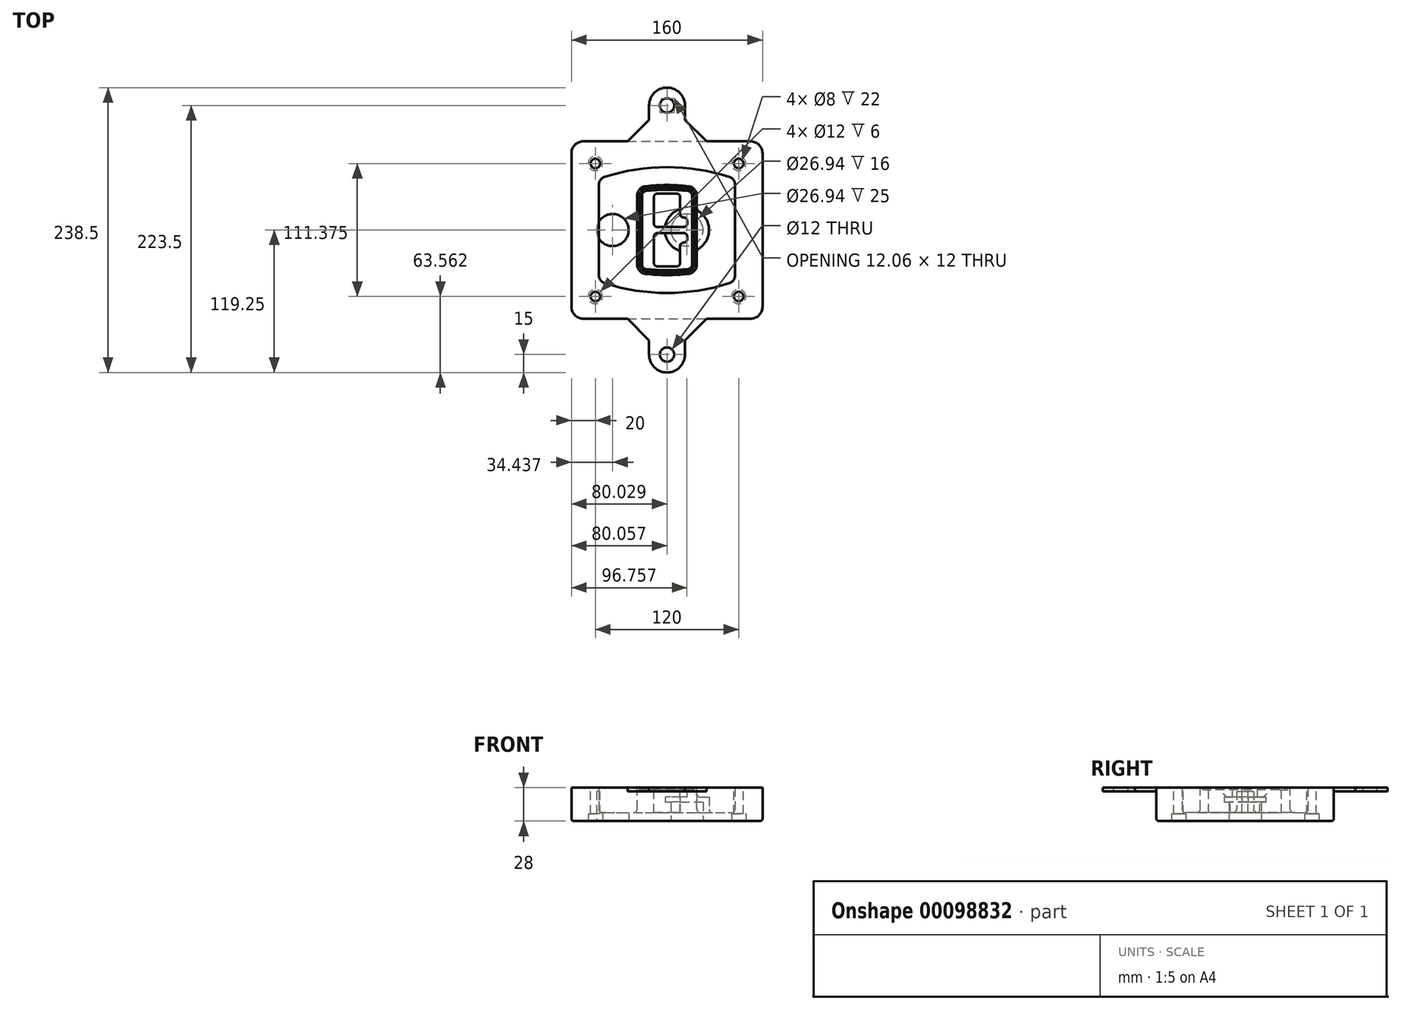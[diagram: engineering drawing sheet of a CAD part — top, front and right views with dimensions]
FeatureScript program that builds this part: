
annotation { "Feature Type Name" : "Feature", "Feature Type Description" : "" }
export const myFeature = defineFeature(function(context is Context, id is Id, definition is map)
    precondition{}
    {
        {
            var Q0;
            Q0=qCreatedBy(makeId("Top.planeOp"),FACE);
            var sketch = newSketch(context, id + "F0", { "sketchPlane" : qUnion([Q0])});
            skPoint(sketch, "E0.rect.middle", {"position": v(0, 0) * mm});
            skLineSegment(sketch, "E1.bottom", {"start": v(-70, -74.25) * mm, "end": v(70, -74.25) * mm});
            skLineSegment(sketch, "E1.top", {"start": v(-70, 74.25) * mm, "end": v(70, 74.25) * mm});
            skLineSegment(sketch, "E1.left", {"start": v(-80, -64.25) * mm, "end": v(-80, 64.25) * mm});
            skLineSegment(sketch, "E1.right", {"start": v(80, -64.25) * mm, "end": v(80, 64.25) * mm});
            skLineSegment(sketch, "E2", {"start": v(-80, 74.25) * mm, "end": v(80, -74.25) * mm, "construction": true});
            skLineSegment(sketch, "E3", {"start": v(80, 74.25) * mm, "end": v(-80, -74.25) * mm, "construction": true});
            skCircle(sketch, "E4", {"center": v(-60, 55.69) * mm, "radius": 4 * mm});
            skCircle(sketch, "E5", {"center": v(60, 55.69) * mm, "radius": 4 * mm});
            skCircle(sketch, "E6", {"center": v(60, -55.69) * mm, "radius": 4 * mm});
            skCircle(sketch, "E7", {"center": v(-60, -55.69) * mm, "radius": 4 * mm});
            skLineSegment(sketch, "E8", {"start": v(-60, 55.69) * mm, "end": v(60, 55.69) * mm, "construction": true});
            skLineSegment(sketch, "E9", {"start": v(60, 55.69) * mm, "end": v(60, -55.69) * mm, "construction": true});
            skLineSegment(sketch, "E10", {"start": v(60, -55.69) * mm, "end": v(-60, -55.69) * mm, "construction": true});
            skLineSegment(sketch, "E11", {"start": v(-60, -55.69) * mm, "end": v(-60, 55.69) * mm, "construction": true});
            skLineSegment(sketch, "E12", {"start": v(-60, 37.87) * mm, "end": v(-60, -37.87) * mm});
            skLineSegment(sketch, "E13", {"start": v(60, 37.87) * mm, "end": v(60, -37.87) * mm});
            skArc(sketch, "E14", {"start": v(53.05, 47.4) * mm, "mid": v(0, 55.69) * mm, "end": v(-53.05, 47.4) * mm});
            skArc(sketch, "E15", {"start": v(-53.05, -47.4) * mm, "mid": v(0, -55.69) * mm, "end": v(53.05, -47.4) * mm});
            skLineSegment(sketch, "E16", {"start": v(-60, 0) * mm, "end": v(60, 0) * mm, "construction": true});
            skPoint(sketch, "E17.visualSharp", {"position": v(-60, -45) * mm});
            skArc(sketch, "E17.filletArc", {"start": v(-60, -37.87) * mm, "mid": v(-58.08, -43.76) * mm, "end": v(-53.05, -47.4) * mm});
            skPoint(sketch, "E18.visualSharp", {"position": v(-60, 45) * mm});
            skArc(sketch, "E18.filletArc", {"start": v(-53.05, 47.4) * mm, "mid": v(-58.08, 43.76) * mm, "end": v(-60, 37.87) * mm});
            skPoint(sketch, "E19.visualSharp", {"position": v(60, 45) * mm});
            skArc(sketch, "E19.filletArc", {"start": v(60, 37.87) * mm, "mid": v(58.08, 43.76) * mm, "end": v(53.05, 47.4) * mm});
            skPoint(sketch, "E20.visualSharp", {"position": v(60, -45) * mm});
            skArc(sketch, "E20.filletArc", {"start": v(53.05, -47.4) * mm, "mid": v(58.08, -43.76) * mm, "end": v(60, -37.87) * mm});
            skPoint(sketch, "E21.visualSharp", {"position": v(-80, 74.25) * mm});
            skArc(sketch, "E21.filletArc", {"start": v(-70, 74.25) * mm, "mid": v(-77.07, 71.32) * mm, "end": v(-80, 64.25) * mm});
            skPoint(sketch, "E22.visualSharp", {"position": v(80, 74.25) * mm});
            skArc(sketch, "E22.filletArc", {"start": v(80, 64.25) * mm, "mid": v(77.07, 71.32) * mm, "end": v(70, 74.25) * mm});
            skPoint(sketch, "E23.visualSharp", {"position": v(80, -74.25) * mm});
            skArc(sketch, "E23.filletArc", {"start": v(70, -74.25) * mm, "mid": v(77.07, -71.32) * mm, "end": v(80, -64.25) * mm});
            skPoint(sketch, "E24.visualSharp", {"position": v(-80, -74.25) * mm});
            skArc(sketch, "E24.filletArc", {"start": v(-80, -64.25) * mm, "mid": v(-77.07, -71.32) * mm, "end": v(-70, -74.25) * mm});
            skArc(sketch, "E25.0", {"start": v(57, 37.87) * mm, "mid": v(55.66, 42) * mm, "end": v(52.14, 44.53) * mm});
            skLineSegment(sketch, "E25.1", {"start": v(57, 37.87) * mm, "end": v(57, -37.87) * mm});
            skArc(sketch, "E25.2", {"start": v(52.14, -44.53) * mm, "mid": v(55.66, -42) * mm, "end": v(57, -37.87) * mm});
            skArc(sketch, "E25.3", {"start": v(-52.14, -44.53) * mm, "mid": v(0, -52.69) * mm, "end": v(52.14, -44.53) * mm});
            skArc(sketch, "E25.4", {"start": v(-57, -37.87) * mm, "mid": v(-55.66, -42) * mm, "end": v(-52.14, -44.53) * mm});
            skArc(sketch, "E25.5", {"start": v(52.14, 44.53) * mm, "mid": v(0, 52.69) * mm, "end": v(-52.14, 44.53) * mm});
            skLineSegment(sketch, "E25.6", {"start": v(-57, 37.87) * mm, "end": v(-57, -37.87) * mm});
            skArc(sketch, "E25.7", {"start": v(-52.14, 44.53) * mm, "mid": v(-55.66, 42) * mm, "end": v(-57, 37.87) * mm});
            skArc(sketch, "E26.0", {"start": v(-54.27, 51.2) * mm, "mid": v(-61.31, 46.12) * mm, "end": v(-64, 37.87) * mm});
            skArc(sketch, "E26.1", {"start": v(54.27, 51.2) * mm, "mid": v(0, 59.69) * mm, "end": v(-54.27, 51.2) * mm});
            skArc(sketch, "E26.2", {"start": v(64, 37.87) * mm, "mid": v(61.31, 46.12) * mm, "end": v(54.27, 51.2) * mm});
            skLineSegment(sketch, "E26.3", {"start": v(64, 37.87) * mm, "end": v(64, -37.87) * mm});
            skArc(sketch, "E26.4", {"start": v(54.27, -51.2) * mm, "mid": v(61.31, -46.12) * mm, "end": v(64, -37.87) * mm});
            skLineSegment(sketch, "E26.5", {"start": v(-64, 37.87) * mm, "end": v(-64, -37.87) * mm});
            skArc(sketch, "E26.6", {"start": v(-54.27, -51.2) * mm, "mid": v(0, -59.69) * mm, "end": v(54.27, -51.2) * mm});
            skArc(sketch, "E26.7", {"start": v(-64, -37.87) * mm, "mid": v(-61.31, -46.12) * mm, "end": v(-54.27, -51.2) * mm});
            skSolve(sketch);
        }
        {
            var Q0;
            Q0=makeQuery(id+"F0.imprint","IMPRINT",FACE,{"disambiguationData":[TD([[makeQuery(id+"F0.imprint","IMPRINT",EDGE,{"derivedFrom":sQuery(id+"F0.wireOp",EDGE,"E1.bottom")}),1.0]])]});
            var Q1;
            Q1=makeQuery(id+"F0.imprint","IMPRINT",FACE,{"disambiguationData":[TD([[makeQuery(id+"F0.imprint","IMPRINT",EDGE,{"derivedFrom":sQuery(id+"F0.wireOp",EDGE,"E12")}),1.0]])]});
            var Q2;
            Q2=makeQuery(id+"F0.imprint","IMPRINT",FACE,{"disambiguationData":[TD([[makeQuery(id+"F0.imprint","IMPRINT",EDGE,{"derivedFrom":sQuery(id+"F0.wireOp",EDGE,"E25.0")}),1.0]])]});
            var Q3;
            Q3=makeQuery(id+"F0.imprint","IMPRINT",FACE,{"disambiguationData":[TD([[makeQuery(id+"F0.imprint","IMPRINT",EDGE,{"derivedFrom":sQuery(id+"F0.wireOp",EDGE,"E12")}),-1.0]])]});
            extrude(context, id + "F1", {"entities" : qUnion([Q0, Q1, Q2, Q3]), "oppositeDirection" : true, "depth" : 25 * mm});
        }
        {
            var Q0;
            Q0=makeQuery(id+"F0.imprint","IMPRINT",FACE,{"disambiguationData":[TD([[makeQuery(id+"F0.imprint","IMPRINT",EDGE,{"derivedFrom":sQuery(id+"F0.wireOp",EDGE,"E12")}),1.0]])]});
            extrude(context, id + "F2", {"entities" : qUnion([Q0]), "operationType" : NewBodyOperationType.ADD, "depth" : 3 * mm});
        }
        {
            var Q0;
            Q0=makeQuery(id+"F0.imprint","IMPRINT",FACE,{"disambiguationData":[TD([[makeQuery(id+"F0.imprint","IMPRINT",EDGE,{"derivedFrom":sQuery(id+"F0.wireOp",EDGE,"E25.0")}),1.0]])]});
            extrude(context, id + "F3", {"entities" : qUnion([Q0]), "operationType" : NewBodyOperationType.REMOVE, "oppositeDirection" : true, "depth" : 18 * mm});
        }
        {
            var Q0;
            Q0=makeQuery(id+"F2.opExtrude","CAP_FACE",FACE,{"disambiguationData":[OSD([sQuery(id+"F0.wireOp",EDGE,"E12"),sQuery(id+"F0.wireOp",EDGE,"E13"),sQuery(id+"F0.wireOp",EDGE,"E14"),sQuery(id+"F0.wireOp",EDGE,"E15"),sQuery(id+"F0.wireOp",EDGE,"E17.filletArc"),sQuery(id+"F0.wireOp",EDGE,"E18.filletArc"),sQuery(id+"F0.wireOp",EDGE,"E19.filletArc"),sQuery(id+"F0.wireOp",EDGE,"E20.filletArc"),sQuery(id+"F0.wireOp",EDGE,"E25.0"),sQuery(id+"F0.wireOp",EDGE,"E25.1"),sQuery(id+"F0.wireOp",EDGE,"E25.2"),sQuery(id+"F0.wireOp",EDGE,"E25.3"),sQuery(id+"F0.wireOp",EDGE,"E25.4"),sQuery(id+"F0.wireOp",EDGE,"E25.5"),sQuery(id+"F0.wireOp",EDGE,"E25.6"),sQuery(id+"F0.wireOp",EDGE,"E25.7")])],"isStart":false});
            var sketch = newSketch(context, id + "F4", { "sketchPlane" : qUnion([Q0])});
            skArc(sketch, "E27.0", {"start": v(-17.92, -36.65) * mm, "mid": v(0, -37.69) * mm, "end": v(17.92, -36.65) * mm});
            skArc(sketch, "E28.0", {"start": v(17.92, 36.65) * mm, "mid": v(0, 37.69) * mm, "end": v(-17.92, 36.65) * mm});
            skLineSegment(sketch, "E29", {"start": v(-25, 28.7) * mm, "end": v(-25, -28.7) * mm});
            skLineSegment(sketch, "E30", {"start": v(25, 28.7) * mm, "end": v(25, -28.7) * mm});
            skLineSegment(sketch, "E31", {"start": v(-25, 35.67) * mm, "end": v(25, 35.67) * mm, "construction": true});
            skLineSegment(sketch, "E32", {"start": v(-25, -35.67) * mm, "end": v(25, -35.67) * mm, "construction": true});
            skPoint(sketch, "E33.visualSharp", {"position": v(-25, 35.67) * mm});
            skArc(sketch, "E33.filletArc", {"start": v(-17.92, 36.65) * mm, "mid": v(-22.97, 34.03) * mm, "end": v(-25, 28.7) * mm});
            skPoint(sketch, "E34.visualSharp", {"position": v(25, 35.67) * mm});
            skArc(sketch, "E34.filletArc", {"start": v(25, 28.7) * mm, "mid": v(22.97, 34.03) * mm, "end": v(17.92, 36.65) * mm});
            skPoint(sketch, "E35.visualSharp", {"position": v(25, -35.67) * mm});
            skArc(sketch, "E35.filletArc", {"start": v(17.92, -36.65) * mm, "mid": v(22.97, -34.03) * mm, "end": v(25, -28.7) * mm});
            skPoint(sketch, "E36.visualSharp", {"position": v(-25, -35.67) * mm});
            skArc(sketch, "E36.filletArc", {"start": v(-25, -28.7) * mm, "mid": v(-22.97, -34.03) * mm, "end": v(-17.92, -36.65) * mm});
            skArc(sketch, "E37.0", {"start": v(52.14, 44.53) * mm, "mid": v(0, 52.69) * mm, "end": v(-52.14, 44.53) * mm});
            skArc(sketch, "E37.1", {"start": v(-52.14, 44.53) * mm, "mid": v(-55.66, 42) * mm, "end": v(-57, 37.87) * mm});
            skLineSegment(sketch, "E37.2", {"start": v(-57, 37.87) * mm, "end": v(-57, -37.87) * mm});
            skArc(sketch, "E37.3", {"start": v(-57, -37.87) * mm, "mid": v(-55.66, -42) * mm, "end": v(-52.14, -44.53) * mm});
            skArc(sketch, "E37.4", {"start": v(-52.14, -44.53) * mm, "mid": v(0, -52.69) * mm, "end": v(52.14, -44.53) * mm});
            skArc(sketch, "E37.5", {"start": v(52.14, -44.53) * mm, "mid": v(55.66, -42) * mm, "end": v(57, -37.87) * mm});
            skLineSegment(sketch, "E37.6", {"start": v(57, 37.87) * mm, "end": v(57, -37.87) * mm});
            skArc(sketch, "E37.7", {"start": v(57, 37.87) * mm, "mid": v(55.66, 42) * mm, "end": v(52.14, 44.53) * mm});
            skLineSegment(sketch, "E38.0", {"start": v(23, 28.7) * mm, "end": v(23, -28.7) * mm});
            skArc(sketch, "E38.1", {"start": v(17.7, -34.67) * mm, "mid": v(21.48, -32.7) * mm, "end": v(23, -28.7) * mm});
            skArc(sketch, "E38.2", {"start": v(-17.7, -34.67) * mm, "mid": v(0, -35.69) * mm, "end": v(17.7, -34.67) * mm});
            skArc(sketch, "E38.3", {"start": v(-23, -28.7) * mm, "mid": v(-21.48, -32.7) * mm, "end": v(-17.7, -34.67) * mm});
            skLineSegment(sketch, "E38.4", {"start": v(-23, 28.7) * mm, "end": v(-23, -28.7) * mm});
            skArc(sketch, "E38.5", {"start": v(23, 28.7) * mm, "mid": v(21.48, 32.7) * mm, "end": v(17.7, 34.67) * mm});
            skArc(sketch, "E38.6", {"start": v(-17.7, 34.67) * mm, "mid": v(-21.48, 32.7) * mm, "end": v(-23, 28.7) * mm});
            skArc(sketch, "E38.7", {"start": v(17.7, 34.67) * mm, "mid": v(0, 35.69) * mm, "end": v(-17.7, 34.67) * mm});
            skArc(sketch, "E39.0", {"start": v(21, 28.7) * mm, "mid": v(19.99, 31.37) * mm, "end": v(17.46, 32.68) * mm});
            skLineSegment(sketch, "E39.1", {"start": v(21, 28.7) * mm, "end": v(21, -28.7) * mm});
            skArc(sketch, "E39.2", {"start": v(17.46, -32.68) * mm, "mid": v(19.99, -31.37) * mm, "end": v(21, -28.7) * mm});
            skArc(sketch, "E39.3", {"start": v(-17.46, -32.68) * mm, "mid": v(0, -33.69) * mm, "end": v(17.46, -32.68) * mm});
            skArc(sketch, "E39.4", {"start": v(-21, -28.7) * mm, "mid": v(-19.99, -31.37) * mm, "end": v(-17.46, -32.68) * mm});
            skArc(sketch, "E39.5", {"start": v(17.46, 32.68) * mm, "mid": v(0, 33.69) * mm, "end": v(-17.46, 32.68) * mm});
            skLineSegment(sketch, "E39.6", {"start": v(-21, 28.7) * mm, "end": v(-21, -28.7) * mm});
            skArc(sketch, "E39.7", {"start": v(-17.46, 32.68) * mm, "mid": v(-19.99, 31.37) * mm, "end": v(-21, 28.7) * mm});
            skLineSegment(sketch, "E40", {"start": v(-25, 0) * mm, "end": v(25, 0) * mm, "construction": true});
            skLineSegment(sketch, "E41", {"start": v(-11, 5.5) * mm, "end": v(-11, 27.5) * mm});
            skLineSegment(sketch, "E42", {"start": v(-8, 30.5) * mm, "end": v(8, 30.5) * mm});
            skLineSegment(sketch, "E43", {"start": v(11, 27.5) * mm, "end": v(11, 13.5) * mm});
            skLineSegment(sketch, "E44", {"start": v(14, 10.5) * mm, "end": v(14, 10.5) * mm});
            skLineSegment(sketch, "E45", {"start": v(17, 7.5) * mm, "end": v(17, 5.5) * mm});
            skLineSegment(sketch, "E46", {"start": v(14, 2.5) * mm, "end": v(-8, 2.5) * mm});
            skPoint(sketch, "E47.visualSharp", {"position": v(-11, 30.5) * mm});
            skArc(sketch, "E47.filletArc", {"start": v(-8, 30.5) * mm, "mid": v(-10.12, 29.62) * mm, "end": v(-11, 27.5) * mm});
            skPoint(sketch, "E48.visualSharp", {"position": v(11, 30.5) * mm});
            skArc(sketch, "E48.filletArc", {"start": v(11, 27.5) * mm, "mid": v(10.12, 29.62) * mm, "end": v(8, 30.5) * mm});
            skPoint(sketch, "E49.visualSharp", {"position": v(11, 10.5) * mm});
            skArc(sketch, "E49.filletArc", {"start": v(11, 13.5) * mm, "mid": v(11.88, 11.38) * mm, "end": v(14, 10.5) * mm});
            skPoint(sketch, "E50.visualSharp", {"position": v(17, 10.5) * mm});
            skArc(sketch, "E50.filletArc", {"start": v(17, 7.5) * mm, "mid": v(16.12, 9.62) * mm, "end": v(14, 10.5) * mm});
            skPoint(sketch, "E51.visualSharp", {"position": v(17, 2.5) * mm});
            skArc(sketch, "E51.filletArc", {"start": v(14, 2.5) * mm, "mid": v(16.12, 3.38) * mm, "end": v(17, 5.5) * mm});
            skPoint(sketch, "E52.visualSharp", {"position": v(-11, 2.5) * mm});
            skArc(sketch, "E52.filletArc", {"start": v(-11, 5.5) * mm, "mid": v(-10.12, 3.38) * mm, "end": v(-8, 2.5) * mm});
            skLineSegment(sketch, "E53.0.MirrorCS", {"start": v(14, -2.5) * mm, "end": v(-8, -2.5) * mm});
            skArc(sketch, "E54.0.MirrorCS", {"start": v(-11, -5.5) * mm, "mid": v(-10.12, -3.38) * mm, "end": v(-8, -2.5) * mm});
            skLineSegment(sketch, "E55.0.MirrorCS", {"start": v(-11, -5.5) * mm, "end": v(-11, -27.5) * mm});
            skArc(sketch, "E56.0.MirrorCS", {"start": v(-8, -30.5) * mm, "mid": v(-10.12, -29.62) * mm, "end": v(-11, -27.5) * mm});
            skLineSegment(sketch, "E57.0.MirrorCS", {"start": v(-8, -30.5) * mm, "end": v(8, -30.5) * mm});
            skArc(sketch, "E58.0.MirrorCS", {"start": v(11, -27.5) * mm, "mid": v(10.12, -29.62) * mm, "end": v(8, -30.5) * mm});
            skLineSegment(sketch, "E59.0.MirrorCS", {"start": v(11, -27.5) * mm, "end": v(11, -13.5) * mm});
            skArc(sketch, "E60.0.MirrorCS", {"start": v(11, -13.5) * mm, "mid": v(11.88, -11.38) * mm, "end": v(14, -10.5) * mm});
            skArc(sketch, "E61.0.MirrorCS", {"start": v(17, -7.5) * mm, "mid": v(16.12, -9.62) * mm, "end": v(14, -10.5) * mm});
            skLineSegment(sketch, "E62.0.MirrorCS", {"start": v(17, -7.5) * mm, "end": v(17, -5.5) * mm});
            skArc(sketch, "E63.0.MirrorCS", {"start": v(14, -2.5) * mm, "mid": v(16.12, -3.38) * mm, "end": v(17, -5.5) * mm});
            skSolve(sketch);
        }
        {
            var Q0;
            Q0=makeQuery(id+"F4.imprint","IMPRINT",FACE,{"disambiguationData":[TD([[makeQuery(id+"F4.imprint","IMPRINT",EDGE,{"derivedFrom":sQuery(id+"F4.wireOp",EDGE,"E27.0")}),1.0]])]});
            var Q1;
            Q1=makeQuery(id+"F4.imprint","IMPRINT",FACE,{"disambiguationData":[TD([[makeQuery(id+"F4.imprint","IMPRINT",EDGE,{"derivedFrom":sQuery(id+"F4.wireOp",EDGE,"E38.0")}),-1.0]])]});
            var Q2;
            Q2=makeQuery(id+"F4.imprint","IMPRINT",FACE,{"disambiguationData":[TD([[makeQuery(id+"F4.imprint","IMPRINT",EDGE,{"derivedFrom":sQuery(id+"F4.wireOp",EDGE,"E39.0")}),1.0]])]});
            extrude(context, id + "F5", {"entities" : qUnion([Q0, Q1, Q2]), "operationType" : NewBodyOperationType.ADD, "endBound" : BoundingType.UP_TO_NEXT, "oppositeDirection" : true, "depth" : 25 * mm});
        }
        {
            var Q0;
            Q0=makeQuery(id+"F4.imprint","IMPRINT",FACE,{"disambiguationData":[TD([[makeQuery(id+"F4.imprint","IMPRINT",EDGE,{"derivedFrom":sQuery(id+"F4.wireOp",EDGE,"E38.0")}),-1.0]])]});
            extrude(context, id + "F6", {"entities" : qUnion([Q0]), "operationType" : NewBodyOperationType.REMOVE, "oppositeDirection" : true, "depth" : 2 * mm});
        }
        {
            var Q0;
            Q0=makeQuery(id+"F1.opExtrude","CAP_FACE",FACE,{"disambiguationData":[OSD([sQuery(id+"F0.wireOp",EDGE,"E1.bottom"),sQuery(id+"F0.wireOp",EDGE,"E1.top"),sQuery(id+"F0.wireOp",EDGE,"E1.left"),sQuery(id+"F0.wireOp",EDGE,"E1.right"),sQuery(id+"F0.wireOp",EDGE,"E4"),sQuery(id+"F0.wireOp",EDGE,"E5"),sQuery(id+"F0.wireOp",EDGE,"E6"),sQuery(id+"F0.wireOp",EDGE,"E7"),sQuery(id+"F0.wireOp",EDGE,"E21.filletArc"),sQuery(id+"F0.wireOp",EDGE,"E22.filletArc"),sQuery(id+"F0.wireOp",EDGE,"E23.filletArc"),sQuery(id+"F0.wireOp",EDGE,"E24.filletArc")])],"isStart":false});
            var sketch = newSketch(context, id + "F7", { "sketchPlane" : qUnion([Q0])});
            skCircle(sketch, "E64", {"center": v(16.76, 0) * mm, "radius": 13.47 * mm});
            skCircle(sketch, "E65", {"center": v(-45.56, 0) * mm, "radius": 13.47 * mm});
            skLineSegment(sketch, "E66", {"start": v(80, 0) * mm, "end": v(-80, 0) * mm});
            skCircle(sketch, "E67", {"center": v(16.76, 0) * mm, "radius": 18.47 * mm});
            skCircle(sketch, "E68", {"center": v(60, -55.69) * mm, "radius": 6 * mm});
            skCircle(sketch, "E69", {"center": v(-60, -55.69) * mm, "radius": 6 * mm});
            skCircle(sketch, "E70", {"center": v(-60, 55.69) * mm, "radius": 6 * mm});
            skCircle(sketch, "E71", {"center": v(60, 55.69) * mm, "radius": 6 * mm});
            skSolve(sketch);
        }
        {
            var Q0;
            {var subQ1=sQuery(id+"F7.wireOp",EDGE,"E66");var subQ4=sQuery(id+"F7.wireOp",EDGE,"E64");var subQ6=makeQuery(id+"F7.imprint","INTERSECT",VERTEX,{"disambiguationData":[OD(0.0)],"derivedFrom":[subQ4,subQ1]});Q0=makeQuery(id+"F7.imprint","IMPRINT",FACE,{"disambiguationData":[TD([[makeQuery(id+"F7.imprint","IMPRINT",EDGE,{"disambiguationData":[TD([[subQ6,-1.0]])],"derivedFrom":subQ4}),-1.0]])]});}
            var Q1;
            {var subQ0=sQuery(id+"F7.wireOp",EDGE,"E66");var subQ1=sQuery(id+"F7.wireOp",EDGE,"E64");var subQ3=makeQuery(id+"F7.imprint","INTERSECT",VERTEX,{"disambiguationData":[OD(0.0)],"derivedFrom":[subQ1,subQ0]});Q1=makeQuery(id+"F7.imprint","IMPRINT",FACE,{"disambiguationData":[TD([[makeQuery(id+"F7.imprint","IMPRINT",EDGE,{"disambiguationData":[TD([[subQ3,-1.0]])],"derivedFrom":subQ1}),1.0]])]});}
            var Q2;
            {var subQ0=sQuery(id+"F7.wireOp",EDGE,"E66");var subQ1=sQuery(id+"F7.wireOp",EDGE,"E64");var subQ3=makeQuery(id+"F7.imprint","INTERSECT",VERTEX,{"disambiguationData":[OD(0.0)],"derivedFrom":[subQ1,subQ0]});Q2=makeQuery(id+"F7.imprint","IMPRINT",FACE,{"disambiguationData":[TD([[makeQuery(id+"F7.imprint","IMPRINT",EDGE,{"disambiguationData":[TD([[subQ3,1.0]])],"derivedFrom":subQ1}),1.0]])]});}
            var Q3;
            {var subQ1=sQuery(id+"F7.wireOp",EDGE,"E66");var subQ4=sQuery(id+"F7.wireOp",EDGE,"E64");var subQ6=makeQuery(id+"F7.imprint","INTERSECT",VERTEX,{"disambiguationData":[OD(0.0)],"derivedFrom":[subQ4,subQ1]});Q3=makeQuery(id+"F7.imprint","IMPRINT",FACE,{"disambiguationData":[TD([[makeQuery(id+"F7.imprint","IMPRINT",EDGE,{"disambiguationData":[TD([[subQ6,1.0]])],"derivedFrom":subQ4}),-1.0]])]});}
            extrude(context, id + "F8", {"entities" : qUnion([Q0, Q1, Q2, Q3]), "operationType" : NewBodyOperationType.ADD, "oppositeDirection" : true, "depth" : 20 * mm});
        }
        {
            var Q0;
            {var subQ0=sQuery(id+"F7.wireOp",EDGE,"E66");var subQ1=sQuery(id+"F7.wireOp",EDGE,"E64");var subQ3=makeQuery(id+"F7.imprint","INTERSECT",VERTEX,{"disambiguationData":[OD(0.0)],"derivedFrom":[subQ1,subQ0]});Q0=makeQuery(id+"F7.imprint","IMPRINT",FACE,{"disambiguationData":[TD([[makeQuery(id+"F7.imprint","IMPRINT",EDGE,{"disambiguationData":[TD([[subQ3,-1.0]])],"derivedFrom":subQ1}),1.0]])]});}
            var Q1;
            {var subQ0=sQuery(id+"F7.wireOp",EDGE,"E66");var subQ1=sQuery(id+"F7.wireOp",EDGE,"E64");var subQ3=makeQuery(id+"F7.imprint","INTERSECT",VERTEX,{"disambiguationData":[OD(0.0)],"derivedFrom":[subQ1,subQ0]});Q1=makeQuery(id+"F7.imprint","IMPRINT",FACE,{"disambiguationData":[TD([[makeQuery(id+"F7.imprint","IMPRINT",EDGE,{"disambiguationData":[TD([[subQ3,1.0]])],"derivedFrom":subQ1}),1.0]])]});}
            extrude(context, id + "F9", {"entities" : qUnion([Q0, Q1]), "operationType" : NewBodyOperationType.REMOVE, "oppositeDirection" : true, "depth" : 16 * mm});
        }
        {
            var Q0;
            {var subQ0=sQuery(id+"F7.wireOp",EDGE,"E66");var subQ1=sQuery(id+"F7.wireOp",EDGE,"E65");var subQ3=makeQuery(id+"F7.imprint","INTERSECT",VERTEX,{"disambiguationData":[OD(0.0)],"derivedFrom":[subQ1,subQ0]});Q0=makeQuery(id+"F7.imprint","IMPRINT",FACE,{"disambiguationData":[TD([[makeQuery(id+"F7.imprint","IMPRINT",EDGE,{"disambiguationData":[TD([[subQ3,-1.0]])],"derivedFrom":subQ1}),1.0]])]});}
            var Q1;
            {var subQ0=sQuery(id+"F7.wireOp",EDGE,"E66");var subQ1=sQuery(id+"F7.wireOp",EDGE,"E65");var subQ3=makeQuery(id+"F7.imprint","INTERSECT",VERTEX,{"disambiguationData":[OD(0.0)],"derivedFrom":[subQ1,subQ0]});Q1=makeQuery(id+"F7.imprint","IMPRINT",FACE,{"disambiguationData":[TD([[makeQuery(id+"F7.imprint","IMPRINT",EDGE,{"disambiguationData":[TD([[subQ3,1.0]])],"derivedFrom":subQ1}),1.0]])]});}
            extrude(context, id + "F10", {"entities" : qUnion([Q0, Q1]), "operationType" : NewBodyOperationType.REMOVE, "oppositeDirection" : true, "depth" : 25 * mm});
        }
        {
            var Q0;
            Q0=makeQuery(id+"F7.imprint","IMPRINT",FACE,{"disambiguationData":[TD([[makeQuery(id+"F7.imprint","IMPRINT",EDGE,{"derivedFrom":sQuery(id+"F7.wireOp",EDGE,"E68")}),1.0]])]});
            var Q1;
            Q1=makeQuery(id+"F7.imprint","IMPRINT",FACE,{"disambiguationData":[TD([[makeQuery(id+"F7.imprint","IMPRINT",EDGE,{"derivedFrom":makeQuery(id+"F1.opExtrude","CAP_EDGE",EDGE,{"disambiguationData":[OSD([sQuery(id+"F0.wireOp",EDGE,"E5")])],"isStart":false})}),-1.0]])]});
            var Q2;
            Q2=makeQuery(id+"F7.imprint","IMPRINT",FACE,{"disambiguationData":[TD([[makeQuery(id+"F7.imprint","IMPRINT",EDGE,{"derivedFrom":sQuery(id+"F7.wireOp",EDGE,"E69")}),1.0]])]});
            var Q3;
            Q3=makeQuery(id+"F7.imprint","IMPRINT",FACE,{"disambiguationData":[TD([[makeQuery(id+"F7.imprint","IMPRINT",EDGE,{"derivedFrom":makeQuery(id+"F1.opExtrude","CAP_EDGE",EDGE,{"disambiguationData":[OSD([sQuery(id+"F0.wireOp",EDGE,"E4")])],"isStart":false})}),-1.0]])]});
            var Q4;
            Q4=makeQuery(id+"F7.imprint","IMPRINT",FACE,{"disambiguationData":[TD([[makeQuery(id+"F7.imprint","IMPRINT",EDGE,{"derivedFrom":sQuery(id+"F7.wireOp",EDGE,"E70")}),1.0]])]});
            var Q5;
            Q5=makeQuery(id+"F7.imprint","IMPRINT",FACE,{"disambiguationData":[TD([[makeQuery(id+"F7.imprint","IMPRINT",EDGE,{"derivedFrom":makeQuery(id+"F1.opExtrude","CAP_EDGE",EDGE,{"disambiguationData":[OSD([sQuery(id+"F0.wireOp",EDGE,"E7")])],"isStart":false})}),-1.0]])]});
            var Q6;
            Q6=makeQuery(id+"F7.imprint","IMPRINT",FACE,{"disambiguationData":[TD([[makeQuery(id+"F7.imprint","IMPRINT",EDGE,{"derivedFrom":sQuery(id+"F7.wireOp",EDGE,"E71")}),1.0]])]});
            var Q7;
            Q7=makeQuery(id+"F7.imprint","IMPRINT",FACE,{"disambiguationData":[TD([[makeQuery(id+"F7.imprint","IMPRINT",EDGE,{"derivedFrom":makeQuery(id+"F1.opExtrude","CAP_EDGE",EDGE,{"disambiguationData":[OSD([sQuery(id+"F0.wireOp",EDGE,"E6")])],"isStart":false})}),-1.0]])]});
            extrude(context, id + "F11", {"entities" : qUnion([Q0, Q1, Q2, Q3, Q4, Q5, Q6, Q7]), "operationType" : NewBodyOperationType.REMOVE, "oppositeDirection" : true, "depth" : 6 * mm});
        }
        {
            var Q0;
            Q0=makeQuery(id+"F9.boolean.opBoolean","COPY",FACE,{"derivedFrom":makeQuery(id+"F9.opExtrude","CAP_FACE",FACE,{"disambiguationData":[OSD([sQuery(id+"F7.wireOp",EDGE,"E64")])],"isStart":false})});
            var sketch = newSketch(context, id + "F12", { "sketchPlane" : qUnion([Q0])});
            skArc(sketch, "E72.0", {"start": v(11, 17.55) * mm, "mid": v(2.57, 11.82) * mm, "end": v(-1.54, 2.5) * mm});
            skArc(sketch, "E72.1", {"start": v(-1.54, -2.5) * mm, "mid": v(2.57, -11.82) * mm, "end": v(11, -17.55) * mm});
            skLineSegment(sketch, "E73", {"start": v(-1.54, -2.5) * mm, "end": v(14, -2.5) * mm});
            skLineSegment(sketch, "E74.0", {"start": v(14, 2.5) * mm, "end": v(-1.54, 2.5) * mm});
            skArc(sketch, "E74.1", {"start": v(14, 2.5) * mm, "mid": v(16.12, 3.38) * mm, "end": v(17, 5.5) * mm});
            skLineSegment(sketch, "E74.2", {"start": v(17, 7.5) * mm, "end": v(17, 5.5) * mm});
            skArc(sketch, "E74.3", {"start": v(17, 7.5) * mm, "mid": v(16.12, 9.62) * mm, "end": v(14, 10.5) * mm});
            skArc(sketch, "E74.4", {"start": v(11, 13.5) * mm, "mid": v(11.88, 11.38) * mm, "end": v(14, 10.5) * mm});
            skLineSegment(sketch, "E74.5", {"start": v(11, 17.55) * mm, "end": v(11, 13.5) * mm});
            skLineSegment(sketch, "E74.7", {"start": v(14, -2.5) * mm, "end": v(-1.54, -2.5) * mm});
            skArc(sketch, "E74.8", {"start": v(14, -2.5) * mm, "mid": v(16.12, -3.38) * mm, "end": v(17, -5.5) * mm});
            skLineSegment(sketch, "E74.9", {"start": v(17, -7.5) * mm, "end": v(17, -5.5) * mm});
            skArc(sketch, "E74.10", {"start": v(17, -7.5) * mm, "mid": v(16.12, -9.62) * mm, "end": v(14, -10.5) * mm});
            skArc(sketch, "E74.11", {"start": v(11, -13.5) * mm, "mid": v(11.88, -11.38) * mm, "end": v(14, -10.5) * mm});
            skLineSegment(sketch, "E74.12", {"start": v(11, -17.55) * mm, "end": v(11, -13.5) * mm});
            skPoint(sketch, "E75.orphan", {"position": v(11, -27.5) * mm});
            skPoint(sketch, "E76.orphan", {"position": v(-8, -2.5) * mm});
            skPoint(sketch, "E77.orphan", {"position": v(-8, 2.5) * mm});
            skPoint(sketch, "E78.orphan", {"position": v(11, 27.5) * mm});
            skSolve(sketch);
        }
        {
            var Q0;
            {var subQ7=sQuery(id+"F12.wireOp",EDGE,"E72.0");var subQ14=sQuery(id+"F12.wireOp",EDGE,"E72.1");var subQ16=sQuery(id+"F12.wireOp",EDGE,"E74.1");var subQ18=sQuery(id+"F12.wireOp",EDGE,"E74.8");Q0=qUnion([makeQuery(id+"F12.imprint","IMPRINT",FACE,{"disambiguationData":[TD([[makeQuery(id+"F12.imprint","IMPRINT",EDGE,{"derivedFrom":subQ7}),1.0]])]}),makeQuery(id+"F12.imprint","IMPRINT",FACE,{"disambiguationData":[TD([[makeQuery(id+"F12.imprint","IMPRINT",EDGE,{"derivedFrom":subQ14}),1.0]])]}),makeQuery(id+"F12.imprint","IMPRINT",FACE,{"disambiguationData":[TD([[makeQuery(id+"F12.imprint","IMPRINT",EDGE,{"derivedFrom":subQ16}),1.0]])]}),makeQuery(id+"F12.imprint","IMPRINT",FACE,{"disambiguationData":[TD([[makeQuery(id+"F12.imprint","IMPRINT",EDGE,{"derivedFrom":subQ18}),-1.0]])]})]);}
            var Q1;
            Q1=makeQuery(id+"F5.boolean.opBoolean","SPLIT",FACE,{"disambiguationData":[TD([makeQuery(id+"F5.opExtrude","SWEPT_FACE",FACE,{"disambiguationData":[OSD([sQuery(id+"F4.wireOp",EDGE,"E41")])]})])],"derivedFrom":makeQuery(id+"F3.boolean.opBoolean","COPY",FACE,{"derivedFrom":makeQuery(id+"F3.opExtrude","CAP_FACE",FACE,{"disambiguationData":[OSD([sQuery(id+"F0.wireOp",EDGE,"E25.0"),sQuery(id+"F0.wireOp",EDGE,"E25.1"),sQuery(id+"F0.wireOp",EDGE,"E25.2"),sQuery(id+"F0.wireOp",EDGE,"E25.3"),sQuery(id+"F0.wireOp",EDGE,"E25.4"),sQuery(id+"F0.wireOp",EDGE,"E25.5"),sQuery(id+"F0.wireOp",EDGE,"E25.6"),sQuery(id+"F0.wireOp",EDGE,"E25.7")])],"isStart":false})})});
            extrude(context, id + "F13", {"entities" : qUnion([Q0]), "operationType" : NewBodyOperationType.REMOVE, "endBound" : BoundingType.UP_TO_SURFACE, "endBoundEntityFace" : qUnion([Q1]), "depth" : 25 * mm});
        }
        {
            var Q0;
            Q0=makeQuery(id+"F3.boolean.opBoolean","COPY",EDGE,{"derivedFrom":makeQuery(id+"F3.opExtrude","CAP_EDGE",EDGE,{"disambiguationData":[OSD([sQuery(id+"F0.wireOp",EDGE,"E25.6")])],"isStart":false})});
            var Q1;
            Q1=makeQuery(id+"F8.boolean.opBoolean","INTERSECT",EDGE,{"derivedFrom":[makeQuery(id+"F5.opExtrude","SWEPT_FACE",FACE,{"disambiguationData":[OSD([sQuery(id+"F4.wireOp",EDGE,"E30")])]}),makeQuery(id+"F8.opExtrude","CAP_FACE",FACE,{"disambiguationData":[OSD([sQuery(id+"F7.wireOp",EDGE,"E67")])],"isStart":false})]});
            var Q2;
            Q2=makeQuery(id+"F8.boolean.opBoolean","INTERSECT",EDGE,{"disambiguationData":[OD(1.0)],"derivedFrom":[makeQuery(id+"F5.opExtrude","SWEPT_FACE",FACE,{"disambiguationData":[OSD([sQuery(id+"F4.wireOp",EDGE,"E30")])]}),makeQuery(id+"F8.opExtrude","SWEPT_FACE",FACE,{"disambiguationData":[OSD([sQuery(id+"F7.wireOp",EDGE,"E67")])]})]});
            var Q3;
            {var subQ0=sQuery(id+"F4.wireOp",EDGE,"E30");Q3=makeQuery(id+"F8.boolean.opBoolean","SPLIT",EDGE,{"disambiguationData":[TD([makeQuery(id+"F5.opExtrude","SWEPT_FACE",FACE,{"disambiguationData":[OSD([sQuery(id+"F4.wireOp",EDGE,"E35.filletArc")])]})])],"derivedFrom":makeQuery(id+"F5.opExtrude","CAP_EDGE",EDGE,{"disambiguationData":[OSD([subQ0])],"isStart":false})});}
            var Q4;
            {var subQ0=sQuery(id+"F0.wireOp",EDGE,"E25.7");var subQ1=sQuery(id+"F0.wireOp",EDGE,"E25.1");var subQ2=sQuery(id+"F0.wireOp",EDGE,"E25.6");var subQ3=sQuery(id+"F0.wireOp",EDGE,"E25.5");var subQ4=sQuery(id+"F0.wireOp",EDGE,"E25.4");var subQ5=sQuery(id+"F0.wireOp",EDGE,"E25.0");var subQ6=sQuery(id+"F0.wireOp",EDGE,"E25.2");var subQ7=sQuery(id+"F0.wireOp",EDGE,"E25.3");Q4=makeQuery(id+"F8.boolean.opBoolean","INTERSECT",EDGE,{"derivedFrom":[makeQuery(id+"F5.boolean.opBoolean","SPLIT",FACE,{"disambiguationData":[TD([makeQuery(id+"F2.opExtrude","SWEPT_FACE",FACE,{"disambiguationData":[OSD([subQ5])]})])],"derivedFrom":makeQuery(id+"F3.boolean.opBoolean","COPY",FACE,{"derivedFrom":makeQuery(id+"F3.opExtrude","CAP_FACE",FACE,{"disambiguationData":[OSD([subQ5,subQ1,subQ6,subQ7,subQ4,subQ3,subQ2,subQ0])],"isStart":false})})}),makeQuery(id+"F8.opExtrude","SWEPT_FACE",FACE,{"disambiguationData":[OSD([sQuery(id+"F7.wireOp",EDGE,"E67")])]})]});}
            var Q5;
            Q5=makeQuery(id+"F8.boolean.opBoolean","INTERSECT",EDGE,{"disambiguationData":[OD(0.0)],"derivedFrom":[makeQuery(id+"F5.opExtrude","SWEPT_FACE",FACE,{"disambiguationData":[OSD([sQuery(id+"F4.wireOp",EDGE,"E30")])]}),makeQuery(id+"F8.opExtrude","SWEPT_FACE",FACE,{"disambiguationData":[OSD([sQuery(id+"F7.wireOp",EDGE,"E67")])]})]});
            fillet(context, id + "F14", {"entities" : qUnion([Q0, Q1, Q2, Q3, Q4, Q5]), "radius" : 3 * mm, "tangentPropagation" : true, "allowEdgeOverflow" : false});
        }
        {
            var Q0;
            Q0=makeQuery(id+"F1.opExtrude","CAP_EDGE",EDGE,{"disambiguationData":[OSD([sQuery(id+"F0.wireOp",EDGE,"E1.bottom")])],"isStart":false});
            fillet(context, id + "F15", {"entities" : qUnion([Q0]), "radius" : 2 * mm, "tangentPropagation" : true, "allowEdgeOverflow" : false});
        }
        {
            var Q0;
            Q0=qCreatedBy(makeId("Top.planeOp"),FACE);
            var sketch = newSketch(context, id + "F16", { "sketchPlane" : qUnion([Q0])});
            skArc(sketch, "E79.0", {"start": v(-70, 74.25) * mm, "mid": v(-77.07, 71.32) * mm, "end": v(-80, 64.25) * mm});
            skArc(sketch, "E79.1", {"start": v(80, 64.25) * mm, "mid": v(77.07, 71.32) * mm, "end": v(70, 74.25) * mm});
            skArc(sketch, "E79.2", {"start": v(70, -74.25) * mm, "mid": v(77.07, -71.32) * mm, "end": v(80, -64.25) * mm});
            skArc(sketch, "E79.3", {"start": v(-80, -64.25) * mm, "mid": v(-77.07, -71.32) * mm, "end": v(-70, -74.25) * mm});
            skLineSegment(sketch, "E79.4", {"start": v(-80, -64.25) * mm, "end": v(-80, 64.25) * mm});
            skLineSegment(sketch, "E79.5", {"start": v(-70, -74.25) * mm, "end": v(70, -74.25) * mm});
            skLineSegment(sketch, "E79.6", {"start": v(80, -64.25) * mm, "end": v(80, 64.25) * mm});
            skLineSegment(sketch, "E79.7", {"start": v(-70, 74.25) * mm, "end": v(70, 74.25) * mm});
            skCircle(sketch, "E79.8", {"center": v(60, 55.69) * mm, "radius": 4 * mm});
            skCircle(sketch, "E79.9", {"center": v(-60, 55.69) * mm, "radius": 4 * mm});
            skArc(sketch, "E79.10", {"start": v(-53.05, 47.4) * mm, "mid": v(-58.08, 43.76) * mm, "end": v(-60, 37.87) * mm});
            skArc(sketch, "E79.11", {"start": v(60, 37.87) * mm, "mid": v(58.08, 43.76) * mm, "end": v(53.05, 47.4) * mm});
            skArc(sketch, "E79.12", {"start": v(53.05, 47.4) * mm, "mid": v(0, 55.69) * mm, "end": v(-53.05, 47.4) * mm});
            skArc(sketch, "E79.13", {"start": v(53.05, -47.4) * mm, "mid": v(58.08, -43.76) * mm, "end": v(60, -37.87) * mm});
            skLineSegment(sketch, "E79.14", {"start": v(60, 37.87) * mm, "end": v(60, -37.87) * mm});
            skArc(sketch, "E79.15", {"start": v(-53.05, -47.4) * mm, "mid": v(0, -55.69) * mm, "end": v(53.05, -47.4) * mm});
            skArc(sketch, "E79.16", {"start": v(-60, -37.87) * mm, "mid": v(-58.08, -43.76) * mm, "end": v(-53.05, -47.4) * mm});
            skLineSegment(sketch, "E79.17", {"start": v(-60, 37.87) * mm, "end": v(-60, -37.87) * mm});
            skCircle(sketch, "E79.18", {"center": v(-60, -55.69) * mm, "radius": 4 * mm});
            skCircle(sketch, "E79.19", {"center": v(60, -55.69) * mm, "radius": 4 * mm});
            skCircle(sketch, "E80", {"center": v(0, 104.25) * mm, "radius": 6 * mm});
            skArc(sketch, "E81", {"start": v(15.03, 104.25) * mm, "mid": v(0.03, 119.25) * mm, "end": v(-14.97, 104.25) * mm});
            skLineSegment(sketch, "E82", {"start": v(-14.97, 104.25) * mm, "end": v(-14.97, 92.25) * mm});
            skLineSegment(sketch, "E83", {"start": v(-14.97, 92.25) * mm, "end": v(-32.97, 74.25) * mm});
            skLineSegment(sketch, "E84", {"start": v(15.03, 104.25) * mm, "end": v(15.03, 92.25) * mm});
            skLineSegment(sketch, "E85", {"start": v(15.03, 92.25) * mm, "end": v(33.03, 74.25) * mm});
            skLineSegment(sketch, "E86", {"start": v(0.03, 104.25) * mm, "end": v(0.03, 74.25) * mm, "construction": true});
            skLineSegment(sketch, "E87", {"start": v(-80, 0) * mm, "end": v(80, 0) * mm});
            skCircle(sketch, "E88.MirrorC", {"center": v(0.06, 104.25) * mm, "radius": 6 * mm});
            skArc(sketch, "E89.MirrorCS", {"start": v(-14.97, 104.25) * mm, "mid": v(0.03, 119.25) * mm, "end": v(15.03, 104.25) * mm});
            skLineSegment(sketch, "E90.MirrorCS", {"start": v(70.06, -74.25) * mm, "end": v(-69.94, -74.25) * mm});
            skLineSegment(sketch, "E91.MirrorCS", {"start": v(-14.97, -92.25) * mm, "end": v(-32.97, -74.25) * mm});
            skLineSegment(sketch, "E92.MirrorCS", {"start": v(15.03, -92.25) * mm, "end": v(33.03, -74.25) * mm});
            skLineSegment(sketch, "E93.MirrorCS", {"start": v(-14.97, -104.25) * mm, "end": v(-14.97, -92.25) * mm});
            skLineSegment(sketch, "E94.MirrorCS", {"start": v(15.03, -104.25) * mm, "end": v(15.03, -92.25) * mm});
            skArc(sketch, "E95.MirrorCS", {"start": v(-14.97, -104.25) * mm, "mid": v(0.03, -119.25) * mm, "end": v(15.03, -104.25) * mm});
            skCircle(sketch, "E96.MirrorC", {"center": v(0.06, -104.25) * mm, "radius": 6 * mm});
            skLineSegment(sketch, "E97.MirrorCS", {"start": v(0.03, -104.25) * mm, "end": v(0.03, -74.25) * mm, "construction": true});
            skSolve(sketch);
        }
        {
            var Q0;
            Q0 = qSketchRegion(id + "F16", true);
            var Q1;
            Q1=makeQuery(id+"F2.opExtrude","CAP_FACE",FACE,{"disambiguationData":[OSD([sQuery(id+"F0.wireOp",EDGE,"E12"),sQuery(id+"F0.wireOp",EDGE,"E13"),sQuery(id+"F0.wireOp",EDGE,"E14"),sQuery(id+"F0.wireOp",EDGE,"E15"),sQuery(id+"F0.wireOp",EDGE,"E17.filletArc"),sQuery(id+"F0.wireOp",EDGE,"E18.filletArc"),sQuery(id+"F0.wireOp",EDGE,"E19.filletArc"),sQuery(id+"F0.wireOp",EDGE,"E20.filletArc"),sQuery(id+"F0.wireOp",EDGE,"E25.0"),sQuery(id+"F0.wireOp",EDGE,"E25.1"),sQuery(id+"F0.wireOp",EDGE,"E25.2"),sQuery(id+"F0.wireOp",EDGE,"E25.3"),sQuery(id+"F0.wireOp",EDGE,"E25.4"),sQuery(id+"F0.wireOp",EDGE,"E25.5"),sQuery(id+"F0.wireOp",EDGE,"E25.6"),sQuery(id+"F0.wireOp",EDGE,"E25.7")])],"isStart":false});
            extrude(context, id + "F17", {"entities" : qUnion([Q0]), "operationType" : NewBodyOperationType.ADD, "endBound" : BoundingType.UP_TO_SURFACE, "endBoundEntityFace" : qUnion([Q1]), "depth" : 25 * mm});
        }
    });
